# Revit family: ACO PitLok_Concrete
name_source: partatom
category: Electrical Equipment
revit_build: Autodesk Revit 2015 (Build: 20140903_1530(x64)
units: mm (PartAtom-declared; Revit-internal decimal feet)

## types (12) — shared parameters
Description = ACO PitLok High Security Trafficable Enclosures
MF number = 337173
Manufacturer = ACO Pty Ltd
Model = ACO PitLok
UF number = G4010.10
lookup_table_name = ACO PitLok

## per-type parameters (varying)
| type | Assembly Code | URL | bottom_length | bottom_width | overall_depth | overall_top_length | overall_top_width | type_index |
| J5 - ACO PitLok - full body |  |  | 704 mm  [stored 2.30971 ft] | 454 mm  [stored 1.4895 ft] | 860 mm | 910 mm  [stored 2.98556 ft] | 660 mm  [stored 2.16535 ft] | 1 |
| J5 - ACO PitLok - split body |  |  | 709 mm  [stored 2.32612 ft] | 460 mm  [stored 1.50919 ft] | 860 mm | 910 mm  [stored 2.98556 ft] | 660 mm  [stored 2.16535 ft] | 2 |
| J600 - ACO PitLok - full body |  |  | 650 mm  [stored 2.13255 ft] | 650 mm  [stored 2.13255 ft] | 860 mm | 805 mm  [stored 2.64108 ft] | 805 mm  [stored 2.64108 ft] | 3 |
| J600 - ACO PitLok - split body |  |  | 655 mm  [stored 2.14895 ft] | 655 mm  [stored 2.14895 ft] | 860 mm | 805 mm  [stored 2.64108 ft] | 805 mm  [stored 2.64108 ft] | 4 |
| J8 - ACO PitLok - full body | D5030800 | acocablemate.com.au | 1345 mm  [stored 4.41273 ft] | 550 mm  [stored 1.80446 ft] | 1055 mm  [stored 3.46129 ft] | 1565 mm  [stored 5.13451 ft] | 770 mm  [stored 2.52625 ft] | 5 |
| J8 - ACO PitLok - split body |  |  | 1350 mm  [stored 4.42913 ft] | 555 mm  [stored 1.82087 ft] | 1055 mm  [stored 3.46129 ft] | 1565 mm  [stored 5.13451 ft] | 770 mm  [stored 2.52625 ft] | 6 |
| J10 - ACO PitLok - full body |  |  | 1948 mm  [stored 6.39108 ft] | 513 mm  [stored 1.68307 ft] | 1070 mm  [stored 3.5105 ft] | 2220 mm  [stored 7.28346 ft] | 760 mm  [stored 2.49344 ft] | 7 |
| J10 - ACO PitLok - split body |  |  | 1984 mm  [stored 6.50919 ft] | 524 mm  [stored 1.71916 ft] | 1070 mm  [stored 3.5105 ft] | 2220 mm  [stored 7.28346 ft] | 760 mm  [stored 2.49344 ft] | 8 |
| J1000 - ACO PitLok - full body |  |  | 1041 mm  [stored 3.41535 ft] | 1041 mm  [stored 3.41535 ft] | 1070 mm  [stored 3.5105 ft] | 1245 mm  [stored 4.08465 ft] | 1245 mm  [stored 4.08465 ft] | 9 |
| J1000 - ACO PitLok - split body |  |  | 1050 mm  [stored 3.44488 ft] | 1050 mm  [stored 3.44488 ft] | 1070 mm  [stored 3.5105 ft] | 1245 mm  [stored 4.08465 ft] | 1245 mm  [stored 4.08465 ft] | 10 |
| J1000H - ACO PitLok - full body |  |  | 1180 mm  [stored 3.87139 ft] | 1180 mm  [stored 3.87139 ft] | 1310 mm  [stored 4.2979 ft] | 1400 mm  [stored 4.59318 ft] | 1400 mm  [stored 4.59318 ft] | 11 |
| J1500H - ACO PitLok - full body |  |  | 1760 mm  [stored 5.77428 ft] | 1760 mm  [stored 5.77428 ft] | 1570 mm | 1400 mm  [stored 4.59318 ft] | 1400 mm  [stored 4.59318 ft] | 12 |

note: [stored X ft] marks values corroborated as IEEE doubles in the binary element streams (Revit-internal decimal feet)

## geometry (parser evidence)
native form markers: Sweep x19
no freeform markers — native parametric forms only
